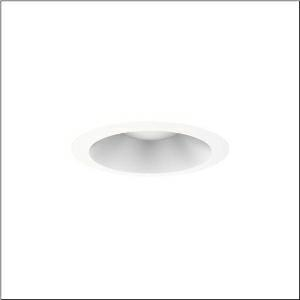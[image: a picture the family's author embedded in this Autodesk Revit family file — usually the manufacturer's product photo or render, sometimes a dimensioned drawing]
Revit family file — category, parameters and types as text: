
# Revit family: lunis_31-xl_51dn15eg32b
name_source: partatom
category: Lighting Fixtures
units: mm (PartAtom-declared; Revit-internal decimal feet)

## family parameters
Cut with Voids When Loaded = No
Host = Face
Light Source = No
Part Type = Normal
Room Calculation Point = No
Round Connector Dimension = Use Diameter
Shared = No

## types (1)
- --- (1 x LED, 2380 lm, 17.5 W, 3000K)
    Apparent Load = 18 VA
    CIE Flux Codes = 89 99 100 100 100
    Color Rendering = 80
    Color Temperature = 3000K
    Default Elevation = 1800 mm
    Description = Lunis 31-XL, downlight, light control with lens, light emission: direct distribution, LED rated luminous flux: 2.380lm, light colour: 830, mains connection: 220..240V, AC/DC, 0/50..60Hz, housing, of aluminium, white, protection rating (complete): IP20, protection rating (on room side): IP54, insulation class (complete): insulation class II (safety insulation), certification: CE, ENEC, packaging unit: 1 piece
    Height = 0 mm  [stored 0 ft]
    Lamp = 1 x LED
    Lamp Light Flux = 2380 lm
    Lamp Power = 17.5 W
    Lamp count = 1
    Length = 259 mm
    Luminous efficacy = 136 lm/W
    Manufacturer = Siteco
    ModVariant = No
    Model = 51DN15EG32B
    Mounting Place = Ceiling
    Mounting Type = Recessed
    Number of Poles = 1
    OnlyDefault = Yes
    Power Factor = 1
    Product Name = Lunis 31-XL
    Product group = downlight
    ProductGroupID = 401
    Protection Class = Protection class II
    Protection Degree = IP 20
    RLX_Detail_Level = 1
    RLX_Emergency_Light_Flux = 0 lm
    RLX_Emergency_Type = 0
    RLX_Emergency_Type_DB = No
    RlxData = <blob elided: 24157 chars, md5=af8f0ac1>
    Socket = socket
    Standby Power = 0 W
    System Light Flux = 2380 lm
    System Power = 18 W
    Type Comments = individual setting: luminous flux: 100 % | (ON | OFF | ON) | 450 mA
    Type Image = l_1345915.jpg
    URL = http://relux.com
    VarID = @adj_029613
    Voltage = 0 V
    Weight = 0.00 kg
    Width = 0 mm  [stored 0 ft]

note: [stored X ft] marks values corroborated as IEEE doubles in the binary element streams (Revit-internal decimal feet)

## geometry (parser evidence)
native form markers: Blend x4, Sweep x10
no freeform markers — native parametric forms only
